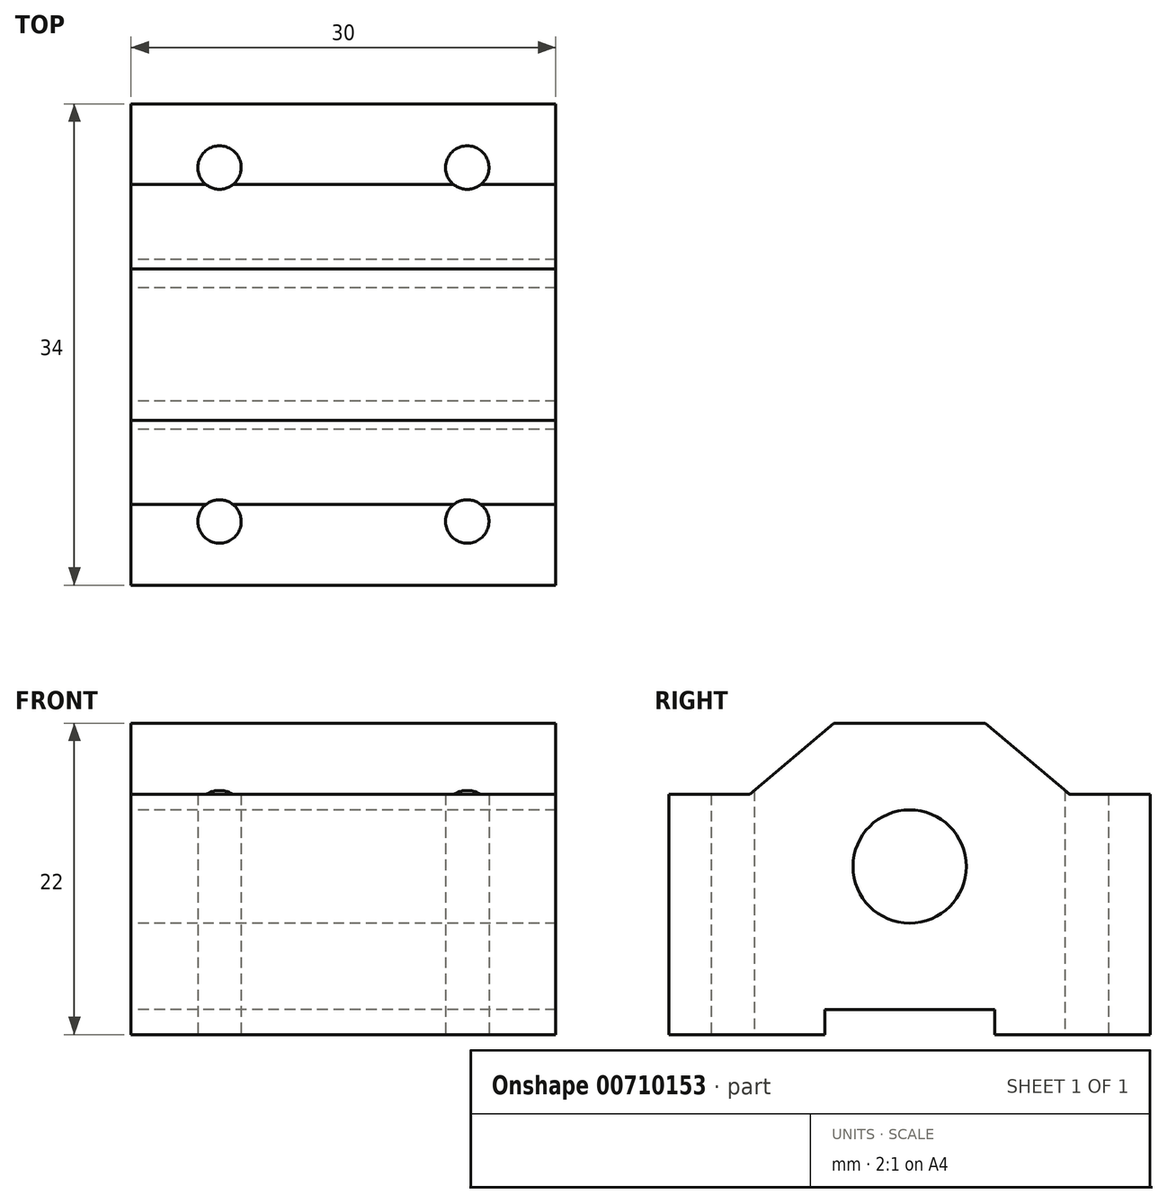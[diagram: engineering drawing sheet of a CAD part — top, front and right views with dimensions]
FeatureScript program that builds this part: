
annotation { "Feature Type Name" : "Feature", "Feature Type Description" : "" }
export const myFeature = defineFeature(function(context is Context, id is Id, definition is map)
    precondition{}
    {
        {
            var Q0;
            Q0=qCreatedBy(makeId("Right.planeOp"),FACE);
            var sketch = newSketch(context, id + "F0", { "sketchPlane" : qUnion([Q0])});
            skLineSegment(sketch, "E0", {"start": v(0, 54.26) * mm, "end": v(0, -67.79) * mm, "construction": true});
            skLineSegment(sketch, "E1.bottom", {"start": v(-5.35, 22) * mm, "end": v(5.35, 22) * mm});
            skLineSegment(sketch, "E1.top", {"start": v(-17, 0) * mm, "end": v(-6, 0) * mm});
            skLineSegment(sketch, "E1.left", {"start": v(-17, 16.96) * mm, "end": v(-17, 0) * mm});
            skLineSegment(sketch, "E1.right", {"start": v(17, 16.96) * mm, "end": v(17, 0) * mm});
            skLineSegment(sketch, "E2.bottom", {"start": v(-6, 1.75) * mm, "end": v(6, 1.75) * mm});
            skLineSegment(sketch, "E2.left", {"start": v(-6, 1.75) * mm, "end": v(-6, 0) * mm});
            skLineSegment(sketch, "E2.right", {"start": v(6, 1.75) * mm, "end": v(6, 0) * mm});
            skLineSegment(sketch, "E3.trimOffspring", {"start": v(6, 0) * mm, "end": v(17, 0) * mm});
            skLineSegment(sketch, "E4", {"start": v(-17, 16.96) * mm, "end": v(-11.3, 16.96) * mm});
            skLineSegment(sketch, "E5", {"start": v(-11.3, 16.96) * mm, "end": v(-5.35, 22) * mm});
            skLineSegment(sketch, "E6.MirrorCS", {"start": v(17, 16.96) * mm, "end": v(11.3, 16.96) * mm});
            skLineSegment(sketch, "E7.MirrorCS", {"start": v(11.3, 16.96) * mm, "end": v(5.35, 22) * mm});
            skPoint(sketch, "E8.orphan", {"position": v(-17, 22) * mm});
            skPoint(sketch, "E9.orphan", {"position": v(17, 22) * mm});
            skLineSegment(sketch, "E10", {"start": v(0, 22) * mm, "end": v(0, 1.75) * mm, "construction": true});
            skCircle(sketch, "E11", {"center": v(0, 11.87) * mm, "radius": 4 * mm});
            skSolve(sketch);
        }
        {
            var Q0;
            Q0 = qSketchRegion(id + "F0", true);
            extrude(context, id + "F1", {"entities" : qUnion([Q0]), "endBound" : BoundingType.SYMMETRIC, "depth" : 30 * mm, "offsetDistance" : 25 * mm});
        }
        {
            var Q0;
            Q0=qCreatedBy(makeId("Top.planeOp"),FACE);
            var sketch = newSketch(context, id + "F2", { "sketchPlane" : qUnion([Q0])});
            skLineSegment(sketch, "E12", {"start": v(0, -22.88) * mm, "end": v(0, 25.47) * mm, "construction": true});
            skLineSegment(sketch, "E13", {"start": v(-20.66, 0) * mm, "end": v(22.74, 0) * mm, "construction": true});
            skCircle(sketch, "E14", {"center": v(-8.75, -12.5) * mm, "radius": 1.53 * mm});
            skCircle(sketch, "E15.MirrorC", {"center": v(-8.75, 12.5) * mm, "radius": 1.53 * mm});
            skCircle(sketch, "E16.MirrorC", {"center": v(8.75, 12.5) * mm, "radius": 1.53 * mm});
            skCircle(sketch, "E17.MirrorC", {"center": v(8.75, -12.5) * mm, "radius": 1.53 * mm});
            skSolve(sketch);
        }
        {
            var Q0;
            Q0 = qSketchRegion(id + "F2", true);
            extrude(context, id + "F3", {"entities" : qUnion([Q0]), "operationType" : NewBodyOperationType.REMOVE, "depth" : 25 * mm, "offsetDistance" : 25 * mm});
        }
    });
